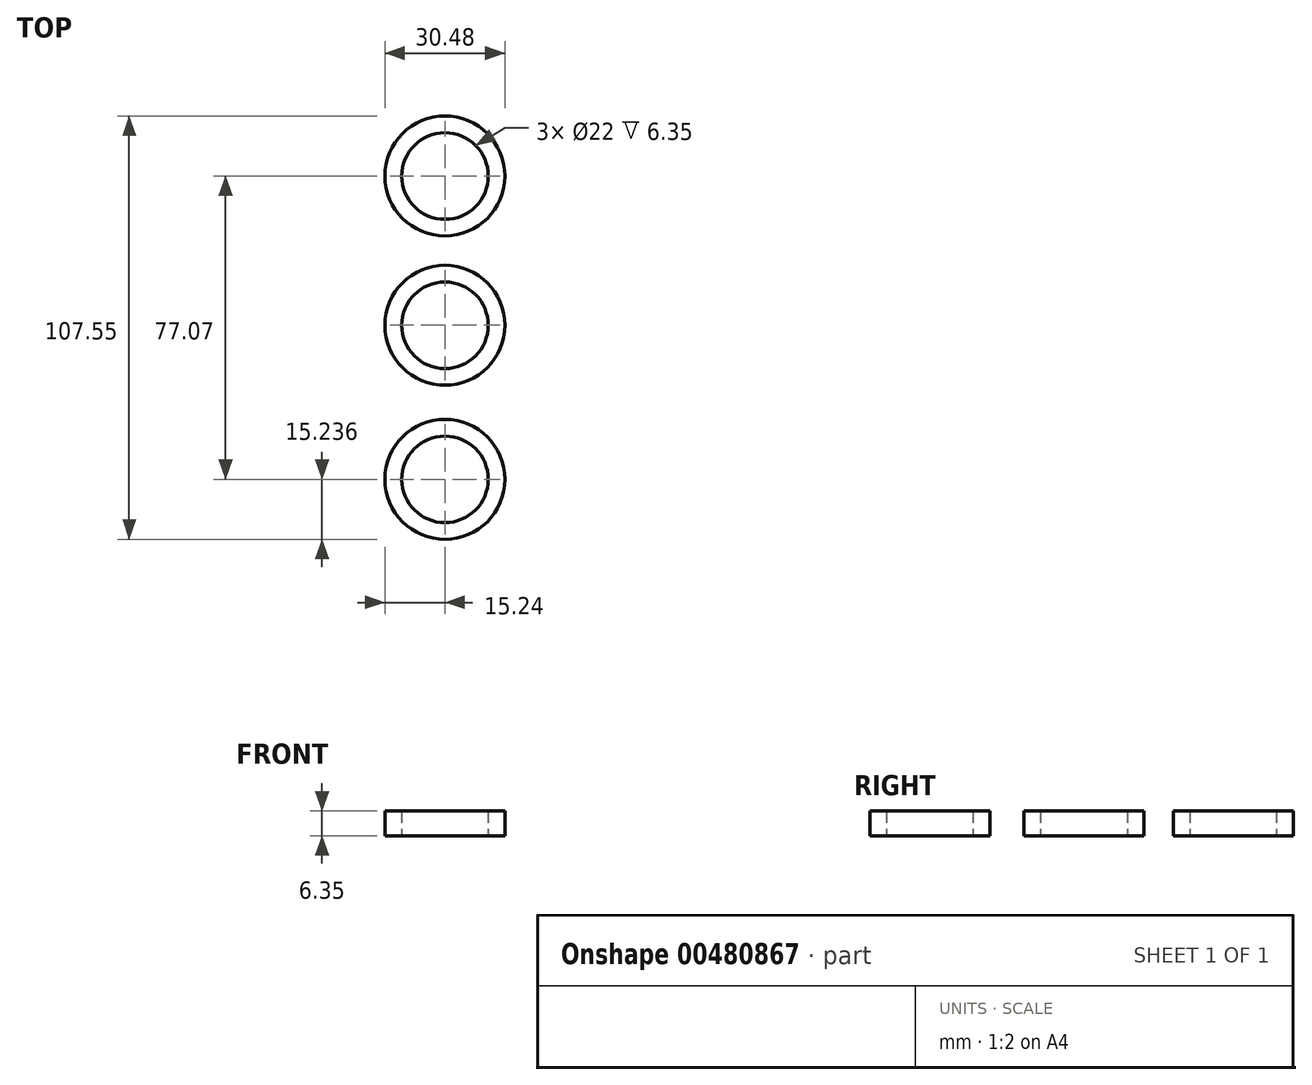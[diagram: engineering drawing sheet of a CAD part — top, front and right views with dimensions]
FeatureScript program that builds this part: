
annotation { "Feature Type Name" : "Feature", "Feature Type Description" : "" }
export const myFeature = defineFeature(function(context is Context, id is Id, definition is map)
    precondition{}
    {
        {
            var Q0;
            Q0=qCreatedBy(makeId("Top.planeOp"),FACE);
            var sketch = newSketch(context, id + "F0", { "sketchPlane" : qUnion([Q0])});
            skCircle(sketch, "E0", {"center": v(0, 0) * mm, "radius": 15.24 * mm});
            skCircle(sketch, "E1", {"center": v(0, 0) * mm, "radius": 11 * mm});
            skCircle(sketch, "E2", {"center": v(0, 37.92) * mm, "radius": 15.24 * mm});
            skCircle(sketch, "E3", {"center": v(0, 37.92) * mm, "radius": 11 * mm});
            skCircle(sketch, "E4", {"center": v(0, -39.15) * mm, "radius": 15.24 * mm});
            skCircle(sketch, "E5", {"center": v(0, -39.15) * mm, "radius": 11 * mm});
            skSolve(sketch);
        }
        {
            var Q0;
            Q0=makeQuery(id+"F0.imprint","IMPRINT",FACE,{"disambiguationData":[TD([[makeQuery(id+"F0.imprint","IMPRINT",EDGE,{"derivedFrom":sQuery(id+"F0.wireOp",EDGE,"E2")}),1.0]])]});
            var Q1;
            Q1=makeQuery(id+"F0.imprint","IMPRINT",FACE,{"disambiguationData":[TD([[makeQuery(id+"F0.imprint","IMPRINT",EDGE,{"derivedFrom":sQuery(id+"F0.wireOp",EDGE,"E0")}),1.0]])]});
            var Q2;
            Q2=makeQuery(id+"F0.imprint","IMPRINT",FACE,{"disambiguationData":[TD([[makeQuery(id+"F0.imprint","IMPRINT",EDGE,{"derivedFrom":sQuery(id+"F0.wireOp",EDGE,"E4")}),1.0]])]});
            var Q3;
            Q3=makeQuery(id+"F0.imprint","IMPRINT",FACE,{"disambiguationData":[TD([[makeQuery(id+"F0.imprint","IMPRINT",EDGE,{"derivedFrom":sQuery(id+"F0.wireOp",EDGE,"E4")}),1.0]])]});
            extrude(context, id + "F1", {"entities" : qUnion([Q0, Q1, Q2, Q3]), "depth" : 6.35 * mm});
        }
    });
